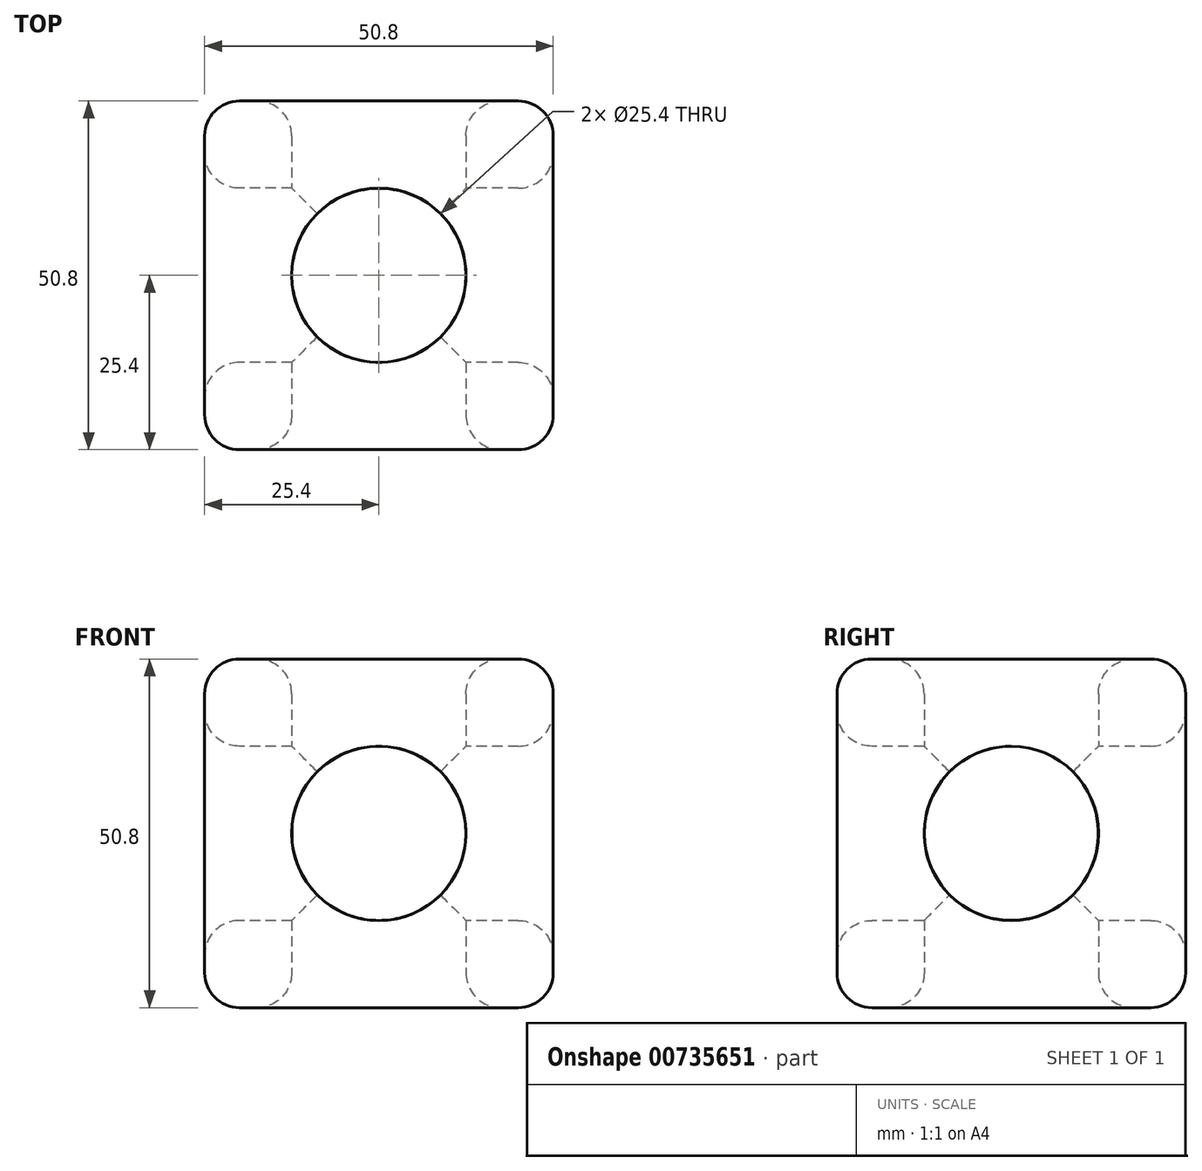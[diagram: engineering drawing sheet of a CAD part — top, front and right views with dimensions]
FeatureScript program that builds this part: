
annotation { "Feature Type Name" : "Feature", "Feature Type Description" : "" }
export const myFeature = defineFeature(function(context is Context, id is Id, definition is map)
    precondition{}
    {
        {
            var Q0;
            Q0=qCreatedBy(makeId("Front.planeOp"),FACE);
            var sketch = newSketch(context, id + "F0", { "sketchPlane" : qUnion([Q0])});
            skLineSegment(sketch, "E0", {"start": v(0, 0) * mm, "end": v(50.8, 0) * mm});
            skLineSegment(sketch, "E1", {"start": v(50.8, 0) * mm, "end": v(50.8, 50.8) * mm});
            skLineSegment(sketch, "E2", {"start": v(50.8, 50.8) * mm, "end": v(0, 50.8) * mm});
            skLineSegment(sketch, "E3", {"start": v(0, 50.8) * mm, "end": v(0, 0) * mm});
            skSolve(sketch);
        }
        {
            var Q0;
            Q0 = qSketchRegion(id + "F0", true);
            extrude(context, id + "F1", {"entities" : qUnion([Q0]), "depth" : 50.8 * mm, "offsetDistance" : 25.4 * mm});
        }
        {
            var Q0;
            Q0=makeQuery(id+"F1.opExtrude","CAP_FACE",FACE,{"disambiguationData":[OSD([sQuery(id+"F0.wireOp",EDGE,"E0"),sQuery(id+"F0.wireOp",EDGE,"E1"),sQuery(id+"F0.wireOp",EDGE,"E2"),sQuery(id+"F0.wireOp",EDGE,"E3")])],"isStart":false});
            var sketch = newSketch(context, id + "F2", { "sketchPlane" : qUnion([Q0])});
            skCircle(sketch, "E4", {"center": v(25.4, 25.4) * mm, "radius": 12.7 * mm});
            skSolve(sketch);
        }
        {
            var Q0;
            Q0=sQuery(id+"F2.wireOp",VERTEX,"E4.center");
            var Q1;
            Q1=makeQuery(id+"F1.opExtrude","SWEPT_BODY",BODY,{"disambiguationData":[OSD([sQuery(id+"F0.wireOp",EDGE,"E0"),sQuery(id+"F0.wireOp",EDGE,"E1"),sQuery(id+"F0.wireOp",EDGE,"E2"),sQuery(id+"F0.wireOp",EDGE,"E3")])]});
            hole(context, id + "F3", {"style" : HoleStyle.SIMPLE, "endStyle" : HoleEndStyle.THROUGH, "holeDiameter" : 25.4 * mm, "majorDiameter" : 6.35 * mm, "isTappedThrough" : true, "tappedDepth" : 12.7 * mm, "tapClearance" : 3, "locations" : qUnion([Q0]), "scope" : qUnion([Q1])});
        }
        {
            var Q0;
            Q0=makeQuery(id+"F1.opExtrude","SWEPT_FACE",FACE,{"disambiguationData":[OSD([sQuery(id+"F0.wireOp",EDGE,"E3")])]});
            var sketch = newSketch(context, id + "F4", { "sketchPlane" : qUnion([Q0])});
            skCircle(sketch, "E5", {"center": v(25.4, 25.4) * mm, "radius": 12.7 * mm});
            skSolve(sketch);
        }
        {
            var Q0;
            Q0=sQuery(id+"F4.wireOp",VERTEX,"E5.center");
            var Q1;
            Q1=makeQuery(id+"F1.opExtrude","SWEPT_BODY",BODY,{"disambiguationData":[OSD([sQuery(id+"F0.wireOp",EDGE,"E0"),sQuery(id+"F0.wireOp",EDGE,"E1"),sQuery(id+"F0.wireOp",EDGE,"E2"),sQuery(id+"F0.wireOp",EDGE,"E3")])]});
            hole(context, id + "F5", {"style" : HoleStyle.SIMPLE, "endStyle" : HoleEndStyle.THROUGH, "holeDiameter" : 25.4 * mm, "majorDiameter" : 6.35 * mm, "isTappedThrough" : true, "tappedDepth" : 12.7 * mm, "tapClearance" : 3, "locations" : qUnion([Q0]), "scope" : qUnion([Q1])});
        }
        {
            var Q0;
            Q0=makeQuery(id+"F1.opExtrude","SWEPT_FACE",FACE,{"disambiguationData":[OSD([sQuery(id+"F0.wireOp",EDGE,"E0")])]});
            var sketch = newSketch(context, id + "F6", { "sketchPlane" : qUnion([Q0])});
            skCircle(sketch, "E6", {"center": v(25.4, 25.4) * mm, "radius": 12.7 * mm});
            skSolve(sketch);
        }
        {
            var Q0;
            Q0=sQuery(id+"F6.wireOp",VERTEX,"E6.center");
            var Q1;
            Q1=makeQuery(id+"F1.opExtrude","SWEPT_BODY",BODY,{"disambiguationData":[OSD([sQuery(id+"F0.wireOp",EDGE,"E0"),sQuery(id+"F0.wireOp",EDGE,"E1"),sQuery(id+"F0.wireOp",EDGE,"E2"),sQuery(id+"F0.wireOp",EDGE,"E3")])]});
            hole(context, id + "F7", {"style" : HoleStyle.SIMPLE, "endStyle" : HoleEndStyle.THROUGH, "holeDiameter" : 25.4 * mm, "majorDiameter" : 6.35 * mm, "isTappedThrough" : true, "tappedDepth" : 12.7 * mm, "tapClearance" : 3, "locations" : qUnion([Q0]), "scope" : qUnion([Q1])});
        }
        {
            var Q0;
            Q0=makeQuery(id+"F1.opExtrude","CAP_FACE",FACE,{"disambiguationData":[OSD([sQuery(id+"F0.wireOp",EDGE,"E0"),sQuery(id+"F0.wireOp",EDGE,"E1"),sQuery(id+"F0.wireOp",EDGE,"E2"),sQuery(id+"F0.wireOp",EDGE,"E3")])],"isStart":false});
            fillet(context, id + "F8", {"entities" : qUnion([Q0]), "radius" : 5.08 * mm, "tangentPropagation" : true, "allowEdgeOverflow" : false});
        }
        {
            var Q0;
            Q0=makeQuery(id+"F1.opExtrude","SWEPT_FACE",FACE,{"disambiguationData":[OSD([sQuery(id+"F0.wireOp",EDGE,"E3")])]});
            fillet(context, id + "F9", {"entities" : qUnion([Q0]), "radius" : 5.08 * mm, "tangentPropagation" : true, "allowEdgeOverflow" : false});
        }
        {
            var Q0;
            Q0=makeQuery(id+"F5.hole-0.boolean.opBoolean","INTERSECT",EDGE,{"derivedFrom":[makeQuery(id+"F1.opExtrude","SWEPT_FACE",FACE,{"disambiguationData":[OSD([sQuery(id+"F0.wireOp",EDGE,"E1")])]}),makeQuery(id+"F5.hole-0.opRevolve","SWEPT_FACE",FACE,{"disambiguationData":[OSD([sQuery(id+"F5.hole-0.sketch.wireOp",EDGE,"core_line_2")])]})]});
            var Q1;
            Q1=makeQuery(id+"F1.opExtrude","SWEPT_FACE",FACE,{"disambiguationData":[OSD([sQuery(id+"F0.wireOp",EDGE,"E1")])]});
            fillet(context, id + "F10", {"entities" : qUnion([Q0, Q1]), "radius" : 5.08 * mm, "tangentPropagation" : true, "allowEdgeOverflow" : false});
        }
        {
            var Q0;
            Q0=makeQuery(id+"F1.opExtrude","CAP_FACE",FACE,{"disambiguationData":[OSD([sQuery(id+"F0.wireOp",EDGE,"E0"),sQuery(id+"F0.wireOp",EDGE,"E1"),sQuery(id+"F0.wireOp",EDGE,"E2"),sQuery(id+"F0.wireOp",EDGE,"E3")])],"isStart":true});
            fillet(context, id + "F11", {"entities" : qUnion([Q0]), "radius" : 5.08 * mm, "tangentPropagation" : true, "allowEdgeOverflow" : false});
        }
        {
            var Q0;
            Q0=makeQuery(id+"F1.opExtrude","SWEPT_FACE",FACE,{"disambiguationData":[OSD([sQuery(id+"F0.wireOp",EDGE,"E2")])]});
            fillet(context, id + "F12", {"entities" : qUnion([Q0]), "radius" : 5.08 * mm, "tangentPropagation" : true, "allowEdgeOverflow" : false});
        }
        {
            var Q0;
            Q0=makeQuery(id+"F1.opExtrude","SWEPT_FACE",FACE,{"disambiguationData":[OSD([sQuery(id+"F0.wireOp",EDGE,"E0")])]});
            fillet(context, id + "F13", {"entities" : qUnion([Q0]), "radius" : 5.08 * mm, "tangentPropagation" : true, "allowEdgeOverflow" : false});
        }
    });
